# Revit family: QF_BPRO_SW 8x5 - 2_569769
name_source: partatom
category: Sonderausstattung
revit_build: Autodesk Revit 2018 (Build: 20190510_1515(x64)
units: mm (PartAtom-declared; Revit-internal decimal feet)

## family parameters
Arbeitsebenenbasiert = Nein
Beim Laden mit Abzugskörper schneiden = Nein
Bemaßung runder Anschluss = Durchmesser verwenden
Gemeinsam genutzt = Nein
Immer vertikal = Ja
Raumberechnungspunkt = Ja
Teiletyp = Normal

## types (1)
- SW 8x5 - 2
    Artikel Nummer = 569769
    Beschreibung = Servierwagen aus rostfreiem Edelstahl
mit 2 Borden 800 x 500 mm
max. Belastung je Bord: 80 kg
Tragfähigkeit: 120 kg
    Beschreibung durch Hersteller analog Leistungsverzeichniskurztext = Abmessungen

Länge:			900 mm
Breite:			600 mm
Höhe:			950 mm

Lichtes Maß:
Höhe zwischen den Borden:	585 mm
Borde:		                       800 x 500 mm

Ausführung

Der Servierwagen besteht aus CNS 18/10, Werkstoff-Nr. 1.4301. Zwischen stabilem Rundrohr mit D = 25 mm befinden sich zwei eingeschweißte tiefgezogene Borde. Die Oberfläche der Borde ist mikroliert. Die Rundrohre an den Stirnseiten werden als Schiebegriffe genutzt. Ein umlaufender 35 mm abgekanteter Profilrand an den Borden, die Rollierung der Bordkante sowie durchgehende Schweißnähte zwischen Rohrrahmen und Borden verstärken die Stabilität des Servierwagens.
Die Borde sind mit einer schalldämmenden Antidröhnmatte unterfüttert.

Der Servierwagen ist fahrbar mittels rostfreien Kunststoffrollen gemäß DIN 18867, Teil 8 (4 Lenkrollen, davon 2 mit Feststeller, Rollendurchmesser 125 mm). Die Rollen sind im Rohrrahmen eingesteckt. Wandabweiser aus Kunststoff (Polyethylen) an allen vier Ecken schützen vor Beschädigung.


Zubehör/ Optionen

• Abfallbehälter AFB 4 x 2 x 2,5 aus CNS, mit Hängevorrichtung, 18,5 Liter (Best.Nr. 555 509)
• Besteckbehälter BGN 1/3-150 aus CNS, mit Hängevorrichtung, 110 Besteckteile 
(Best.Nr. 555 510)
• Galerie umlaufend, 50 mm hoch 
• Knotenbleche zur Stärkung der Stabiliät
• Bordverstärkungsprofile (Wenn Bordverstärkungsprofil, keine Antidröhnmatte enthalten) 
• Luftidentische Rollen, 4 Lenkrollen, davon 2 mit Feststeller, Durchmesser 125 mm
Verkleidungs-Sets:

• Verkleidung 3-seitig aus Edelstahl, zum Einhängen an Servierwagen, Best.Nr.: 375449
• Verkleidung 3-seitig mit frontseitigen Flügeltüren aus Edelstahl, zur einfachen Montage an Servierwagen, Best.Nr.: 375450 (nicht möglich in Kombination mit Knotenblechen)
• Verkleidung 3-seitig aus Feinblech, doppelseitig elektrolytisch verzinkt, pulverbeschichtet in verschiedenen Farben, zum Einhängen an Servierwagen, Best.Nr.: 375453
• Verkleidung 3-seitig mit frontseitigen Flügeltüren aus Feinblech, doppelseitig elektrolytisch verzinkt, pulverbeschichtet in verschiedenen Farben, zur einfachen Montage an Servierwagen, Best.Nr.: 375454 (nicht möglich in Kombination mit Knotenblechen)

Mobile Arbeitsfläche:

• Arbeitsplatte WB 8 x 5 aus CNS zum Aufsetzen auf dem Servierwagen 8 x 5 inkl. Ausschnitt für zwei GN-Behälter 1/3-65; 2x GN 1/3-65 im Lieferumfang enthalten 
(Best.Nr. 574 773)
• Schneidbrett 1/1 aus Kunststoff mit gefräster Saftrinne und Auslauf in die GN-Behälter (Best.Nr. 574 776) 
• Schneidbrett 1/1 aus massiver Buche mit gefräster Saftrinne und Auslauf in die GN-Behälter (Best.Nr. 574 775) 
• Einhängerahmen für GN-Behälter aus CNS inkl. Bügel für Küchenpapierrolle (Best.Nr. 574 783) 
Bietet Platz für bis zu 3 Gastronorm-Behältern GN 1/6 
• Messerhalter aus Kunststoff 114x162x20 zum Aufsetzen auf GN 1/6 (Best.Nr. 574 774)
• Hustenschutz SW SG aus Acrylglas (PMMA), zur einfachen Montage auf den Rohrbügeln (Best.Nr. 574 782)
• Arbeitsplatten-Set Kunststoff, bestehend aus: Arbeitsplatte WB 8x5 inkl. 2x GN 1/3-65, Schneidbrett Kunststoff 1/1, Einhängerahmen inkl. Bügel für Küchenpapierrolle, 1x GN 1/6-200, 1x GN 1/3-200, Messerhalter
(Best.Nr. 574 778)
• Arbeitsplatten-Set Holz, bestehend aus: Arbeitsplatte WB 8x5 inkl. 2x GN 1/3-65, 
Schneidbrett Holz 1/1, Einhängerahmen inkl. Bügel für Küchenpapierrolle, 1x GN 1/6-200, 1x GN 1/3-200, Messerhalter
(Best.Nr. 574 777)


Technische Daten

Werkstoff:	Chromnickelstahl 18/10,
		Polyamid (PA)
Gewicht:		12,44 kg
Tragfähigkeit je Wagen:	120 kg
Tragfähigkeit je Bord:                       80 kg
Anzahl der Borde:		 2


Besonderheit

• Umlaufender Profilrand an den Borden zur Verstärkung der Stabilität des Servierwagens und Verhinderung von seitlichem Abrutschen der abgestellten Gegenstände

• Rollierung der Bordkante: eingerollte Kanten sorgen für hohe Stabilität und schützen das Personal vor Verletzungen.


Fabrikat

Hersteller:                   B.PRO
Typ:                                   SW 8x5-2
Best.Nr.	                     569 769
    Beschreibung durch Hersteller analog Leistungsverzeichnislangtext = Abmessungen

Länge:			900 mm
Breite:			600 mm
Höhe:			950 mm

Lichtes Maß:
Höhe zwischen den Borden:	585 mm
Borde:		                       800 x 500 mm

Ausführung

Der Servierwagen besteht aus CNS 18/10, Werkstoff-Nr. 1.4301. Zwischen stabilem Rundrohr mit D = 25 mm befinden sich zwei eingeschweißte tiefgezogene Borde. Die Oberfläche der Borde ist mikroliert. Die Rundrohre an den Stirnseiten werden als Schiebegriffe genutzt. Ein umlaufender 35 mm abgekanteter Profilrand an den Borden, die Rollierung der Bordkante sowie durchgehende Schweißnähte zwischen Rohrrahmen und Borden verstärken die Stabilität des Servierwagens.
Die Borde sind mit einer schalldämmenden Antidröhnmatte unterfüttert.

Der Servierwagen ist fahrbar mittels rostfreien Kunststoffrollen gemäß DIN 18867, Teil 8 (4 Lenkrollen, davon 2 mit Feststeller, Rollendurchmesser 125 mm). Die Rollen sind im Rohrrahmen eingesteckt. Wandabweiser aus Kunststoff (Polyethylen) an allen vier Ecken schützen vor Beschädigung.


Zubehör/ Optionen

• Abfallbehälter AFB 4 x 2 x 2,5 aus CNS, mit Hängevorrichtung, 18,5 Liter (Best.Nr. 555 509)
• Besteckbehälter BGN 1/3-150 aus CNS, mit Hängevorrichtung, 110 Besteckteile 
(Best.Nr. 555 510)
• Galerie umlaufend, 50 mm hoch 
• Knotenbleche zur Stärkung der Stabiliät
• Bordverstärkungsprofile (Wenn Bordverstärkungsprofil, keine Antidröhnmatte enthalten) 
• Luftidentische Rollen, 4 Lenkrollen, davon 2 mit Feststeller, Durchmesser 125 mm
Verkleidungs-Sets:

• Verkleidung 3-seitig aus Edelstahl, zum Einhängen an Servierwagen, Best.Nr.: 375449
• Verkleidung 3-seitig mit frontseitigen Flügeltüren aus Edelstahl, zur einfachen Montage an Servierwagen, Best.Nr.: 375450 (nicht möglich in Kombination mit Knotenblechen)
• Verkleidung 3-seitig aus Feinblech, doppelseitig elektrolytisch verzinkt, pulverbeschichtet in verschiedenen Farben, zum Einhängen an Servierwagen, Best.Nr.: 375453
• Verkleidung 3-seitig mit frontseitigen Flügeltüren aus Feinblech, doppelseitig elektrolytisch verzinkt, pulverbeschichtet in verschiedenen Farben, zur einfachen Montage an Servierwagen, Best.Nr.: 375454 (nicht möglich in Kombination mit Knotenblechen)

Mobile Arbeitsfläche:

• Arbeitsplatte WB 8 x 5 aus CNS zum Aufsetzen auf dem Servierwagen 8 x 5 inkl. Ausschnitt für zwei GN-Behälter 1/3-65; 2x GN 1/3-65 im Lieferumfang enthalten 
(Best.Nr. 574 773)
• Schneidbrett 1/1 aus Kunststoff mit gefräster Saftrinne und Auslauf in die GN-Behälter (Best.Nr. 574 776) 
• Schneidbrett 1/1 aus massiver Buche mit gefräster Saftrinne und Auslauf in die GN-Behälter (Best.Nr. 574 775) 
• Einhängerahmen für GN-Behälter aus CNS inkl. Bügel für Küchenpapierrolle (Best.Nr. 574 783) 
Bietet Platz für bis zu 3 Gastronorm-Behältern GN 1/6 
• Messerhalter aus Kunststoff 114x162x20 zum Aufsetzen auf GN 1/6 (Best.Nr. 574 774)
• Hustenschutz SW SG aus Acrylglas (PMMA), zur einfachen Montage auf den Rohrbügeln (Best.Nr. 574 782)
• Arbeitsplatten-Set Kunststoff, bestehend aus: Arbeitsplatte WB 8x5 inkl. 2x GN 1/3-65, Schneidbrett Kunststoff 1/1, Einhängerahmen inkl. Bügel für Küchenpapierrolle, 1x GN 1/6-200, 1x GN 1/3-200, Messerhalter
(Best.Nr. 574 778)
• Arbeitsplatten-Set Holz, bestehend aus: Arbeitsplatte WB 8x5 inkl. 2x GN 1/3-65, 
Schneidbrett Holz 1/1, Einhängerahmen inkl. Bügel für Küchenpapierrolle, 1x GN 1/6-200, 1x GN 1/3-200, Messerhalter
(Best.Nr. 574 777)


Technische Daten

Werkstoff:	Chromnickelstahl 18/10,
		Polyamid (PA)
Gewicht:		12,44 kg
Tragfähigkeit je Wagen:	120 kg
Tragfähigkeit je Bord:                       80 kg
Anzahl der Borde:		 2


Besonderheit

• Umlaufender Profilrand an den Borden zur Verstärkung der Stabilität des Servierwagens und Verhinderung von seitlichem Abrutschen der abgestellten Gegenstände

• Rollierung der Bordkante: eingerollte Kanten sorgen für hohe Stabilität und schützen das Personal vor Verletzungen.


Fabrikat

Hersteller:                   B.PRO
Typ:                                   SW 8x5-2
Best.Nr.	                     569 769
    Breite Korpus = 500 mm  [stored 1.64042 ft]
    Gerätegewicht Netto = 12.40 kg
    Großküchengerätezuordnung = Ja
    Hersteller = B.PRO GmbH
    Höhe = 950 mm
    Internetadresse Gerätehersteller = https://www.bpro-solutions.com
    Internetadresse für Ersatzteilliste = https://www.bpro-solutions.com
    Kosten = 334.4 $
    Länge Gerätebreite = 900 mm
    Länge Korpus = 800 mm  [stored 2.62467 ft]
    Material = QF_Metal-Stainless-Steel_general
    Material_Stoßschutz = QF_Rubber-Black-Matt
    Modell = SW 8x5 - 2
    Sockelhöhe = 180 mm  [stored 0.590551 ft]
    Tiefe = 600 mm  [stored 1.9685 ft]
    Typenkommentare = Servierwagen 2-teilig 800 mm
    URL = https://www.bpro-solutions.com
    Warnhinweise = Ausführliche Gefahrenhinweise entnehmen Sie der Betriebsanleitung.
    Zubehör = Nein

note: [stored X ft] marks values corroborated as IEEE doubles in the binary element streams (Revit-internal decimal feet)
